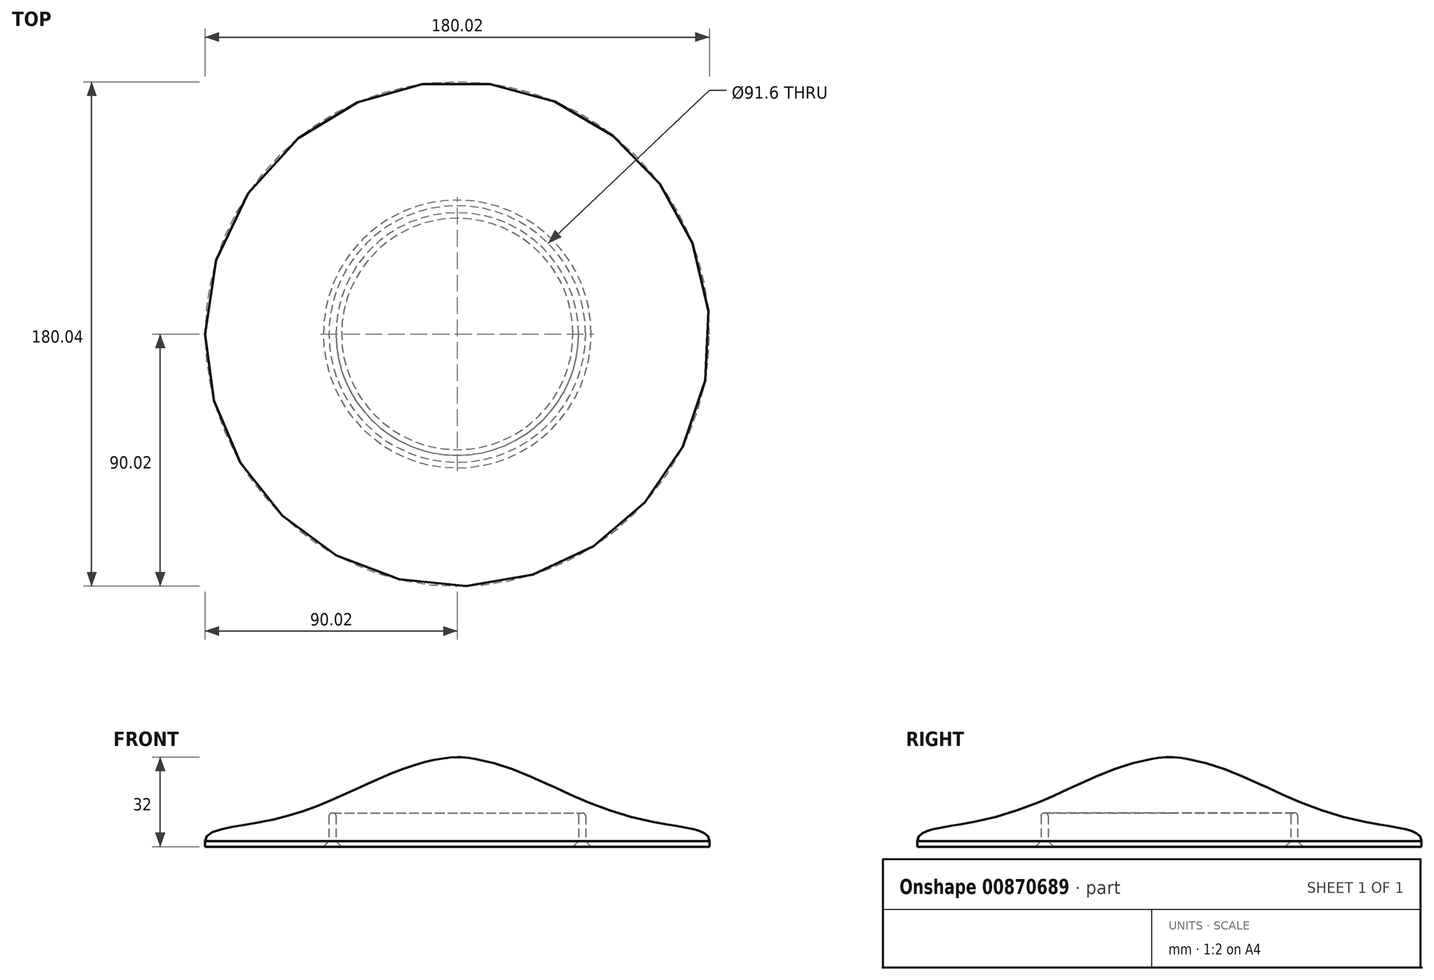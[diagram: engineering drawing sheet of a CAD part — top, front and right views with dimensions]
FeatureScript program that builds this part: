
annotation { "Feature Type Name" : "Feature", "Feature Type Description" : "" }
export const myFeature = defineFeature(function(context is Context, id is Id, definition is map)
    precondition{}
    {
        {
            var Q0;
            Q0=qCreatedBy(makeId("Front.planeOp"),FACE);
            var sketch = newSketch(context, id + "F0", { "sketchPlane" : qUnion([Q0])});
            skLineSegment(sketch, "E0", {"start": v(-45.8, 11) * mm, "end": v(-45.8, 0) * mm});
            skLineSegment(sketch, "E1", {"start": v(-45.8, 0) * mm, "end": v(-90, 0) * mm});
            skLineSegment(sketch, "E2", {"start": v(-90, 0) * mm, "end": v(-90, 2) * mm});
            skFitSpline(sketch, "E3", {"points": [v(-90, 2) * mm, v(-64.9, 9.85) * mm, v(-20.91, 27.2) * mm, v(0, 32) * mm], "startDerivative": vector(-5.19, 47.2) * mm, "endDerivative": vector(52.96, 0.85) * mm});
            skLineSegment(sketch, "E4", {"start": v(-44.8, 12) * mm, "end": v(-44.3, 12) * mm});
            skLineSegment(sketch, "E5", {"start": v(-43.3, 11) * mm, "end": v(-43.3, 0) * mm});
            skLineSegment(sketch, "E6", {"start": v(-43.3, 0) * mm, "end": v(0, 0) * mm});
            skPoint(sketch, "E7.visualSharp", {"position": v(-45.8, 12) * mm});
            skArc(sketch, "E7.filletArc", {"start": v(-44.8, 12) * mm, "mid": v(-45.5, 11.7) * mm, "end": v(-45.8, 11) * mm});
            skPoint(sketch, "E8.visualSharp", {"position": v(-43.3, 12) * mm});
            skArc(sketch, "E8.filletArc", {"start": v(-43.3, 11) * mm, "mid": v(-43.6, 11.7) * mm, "end": v(-44.3, 12) * mm});
            skLineSegment(sketch, "E9", {"start": v(0, 0) * mm, "end": v(0, 38.68) * mm, "construction": true});
            skLineSegment(sketch, "E10", {"start": v(0, 32) * mm, "end": v(0, 0) * mm});
            skSolve(sketch);
        }
        {
            var Q0;
            Q0 = qSketchRegion(id + "F0", true);
            var Q1;
            Q1=sQuery(id+"F0.wireOp",EDGE,"E9");
            revolve(context, id + "F1", {"surfaceOperationType" : NewSurfaceOperationType.NEW, "entities" : qUnion([Q0]), "axis" : qUnion([Q1]), "revolveType" : RevolveType.FULL});
        }
        {
            var Q0;
            Q0=makeQuery(id+"F1.opRevolve","SWEPT_EDGE",EDGE,{"disambiguationData":[OSD([sQuery(id+"F0.wireOp",EDGE,"E5"),sQuery(id+"F0.wireOp",EDGE,"E6")])]});
            var Q1;
            Q1=makeQuery(id+"F1.opRevolve","SWEPT_EDGE",EDGE,{"disambiguationData":[OSD([sQuery(id+"F0.wireOp",EDGE,"E0"),sQuery(id+"F0.wireOp",EDGE,"E1")])]});
            chamfer(context, id + "F2", {"entities" : qUnion([Q0, Q1]), "width" : 2 * mm, "tangentPropagation" : true});
        }
    });
